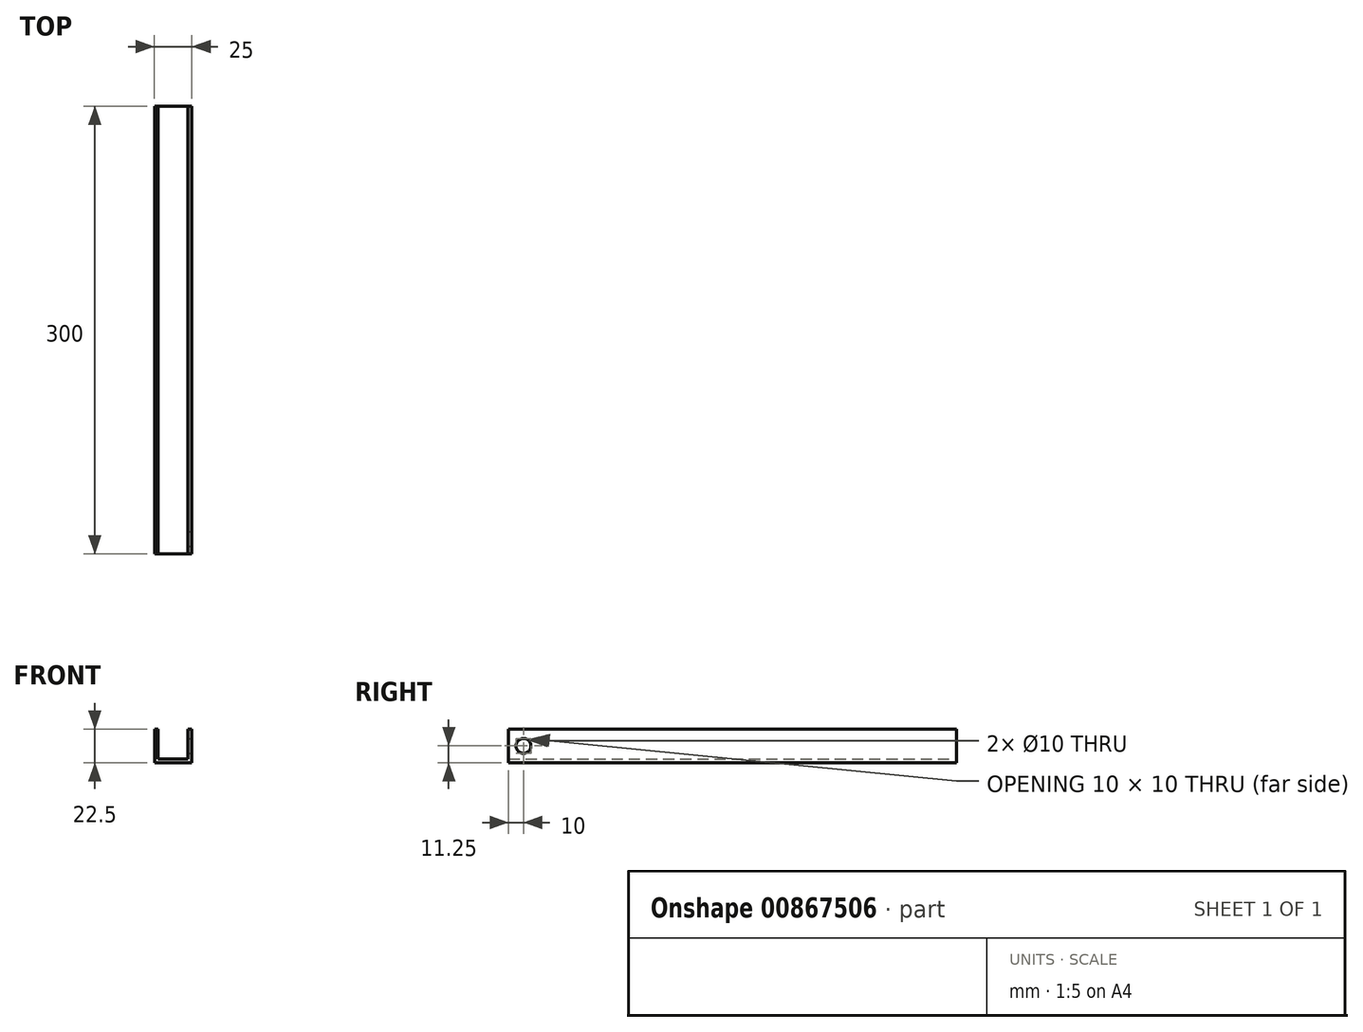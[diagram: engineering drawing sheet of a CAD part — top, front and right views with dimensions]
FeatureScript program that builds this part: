
annotation { "Feature Type Name" : "Feature", "Feature Type Description" : "" }
export const myFeature = defineFeature(function(context is Context, id is Id, definition is map)
    precondition{}
    {
        {
            var Q0;
            Q0=qCreatedBy(makeId("Front.planeOp"),FACE);
            var sketch = newSketch(context, id + "F0", { "sketchPlane" : qUnion([Q0])});
            skLineSegment(sketch, "E0.bottom", {"start": v(-74.99, 0) * mm, "end": v(-49.99, 0) * mm});
            skLineSegment(sketch, "E0.top", {"start": v(-74.99, 22.5) * mm, "end": v(-72.49, 22.5) * mm});
            skLineSegment(sketch, "E0.left", {"start": v(-74.99, 0) * mm, "end": v(-74.99, 22.5) * mm});
            skLineSegment(sketch, "E1.top", {"start": v(-52.49, 2.5) * mm, "end": v(-72.49, 2.5) * mm});
            skLineSegment(sketch, "E2", {"start": v(-72.49, 20) * mm, "end": v(-72.49, 2.5) * mm});
            skLineSegment(sketch, "E3.right", {"start": v(-52.49, 20) * mm, "end": v(-52.49, 2.5) * mm});
            skLineSegment(sketch, "E4", {"start": v(-49.99, 22.5) * mm, "end": v(-49.99, 0) * mm});
            skLineSegment(sketch, "E5", {"start": v(-72.49, 20) * mm, "end": v(-72.49, 22.5) * mm});
            skLineSegment(sketch, "E6", {"start": v(-52.49, 20) * mm, "end": v(-52.49, 22.5) * mm});
            skLineSegment(sketch, "E7.trimOffspring", {"start": v(-52.49, 22.5) * mm, "end": v(-49.99, 22.5) * mm});
            skSolve(sketch);
        }
        {
            var Q0;
            Q0=makeQuery(id+"F0.imprint","IMPRINT",FACE,{"disambiguationData":[TD([[makeQuery(id+"F0.imprint","IMPRINT",EDGE,{"derivedFrom":sQuery(id+"F0.wireOp",EDGE,"E0.bottom")}),1.0]])]});
            extrude(context, id + "F1", {"entities" : qUnion([Q0]), "depth" : 300 * mm, "offsetDistance" : 25 * mm});
        }
        {
            var Q0;
            Q0=qCreatedBy(makeId("Top.planeOp"),FACE);
            var sketch = newSketch(context, id + "F2", { "sketchPlane" : qUnion([Q0])});
            skCircle(sketch, "E8", {"center": v(-62.48, -9.6) * mm, "radius": 5 * mm});
            skCircle(sketch, "E9", {"center": v(-62.48, -39.6) * mm, "radius": 5 * mm});
            skLineSegment(sketch, "E10.0", {"start": v(0, -149.6) * mm, "end": v(-82.52, -149.6) * mm, "construction": true});
            skCircle(sketch, "E11.MirrorC", {"center": v(-62.48, -259.6) * mm, "radius": 5 * mm});
            skCircle(sketch, "E12.MirrorC", {"center": v(-62.48, -289.6) * mm, "radius": 5 * mm});
            skSolve(sketch);
        }
        {
            var Q0;
            Q0=makeQuery(id+"F1.opExtrude","SWEPT_FACE",FACE,{"disambiguationData":[OSD([sQuery(id+"F0.wireOp",EDGE,"E4")])]});
            cPlane(context, id + "F3", {"entities" : qUnion([Q0]), "cplaneType" : CPlaneType.OFFSET, "offset" : 25 * mm, "width" : 150 * mm, "height" : 150 * mm});
        }
        {
            var Q0;
            Q0=qCreatedBy(id+"F3.planeOp",FACE);
            var sketch = newSketch(context, id + "F4", { "sketchPlane" : qUnion([Q0])});
            skCircle(sketch, "E13", {"center": v(-290, 11.25) * mm, "radius": 5 * mm});
            skSolve(sketch);
        }
        {
            var Q0;
            Q0=makeQuery(id+"F4.imprint","IMPRINT",FACE,{"disambiguationData":[TD([[makeQuery(id+"F4.imprint","IMPRINT",EDGE,{"derivedFrom":sQuery(id+"F4.wireOp",EDGE,"E13")}),1.0]])]});
            extrude(context, id + "F5", {"entities" : qUnion([Q0]), "operationType" : NewBodyOperationType.REMOVE, "oppositeDirection" : true, "depth" : 84 * mm, "offsetDistance" : 25 * mm});
        }
    });
